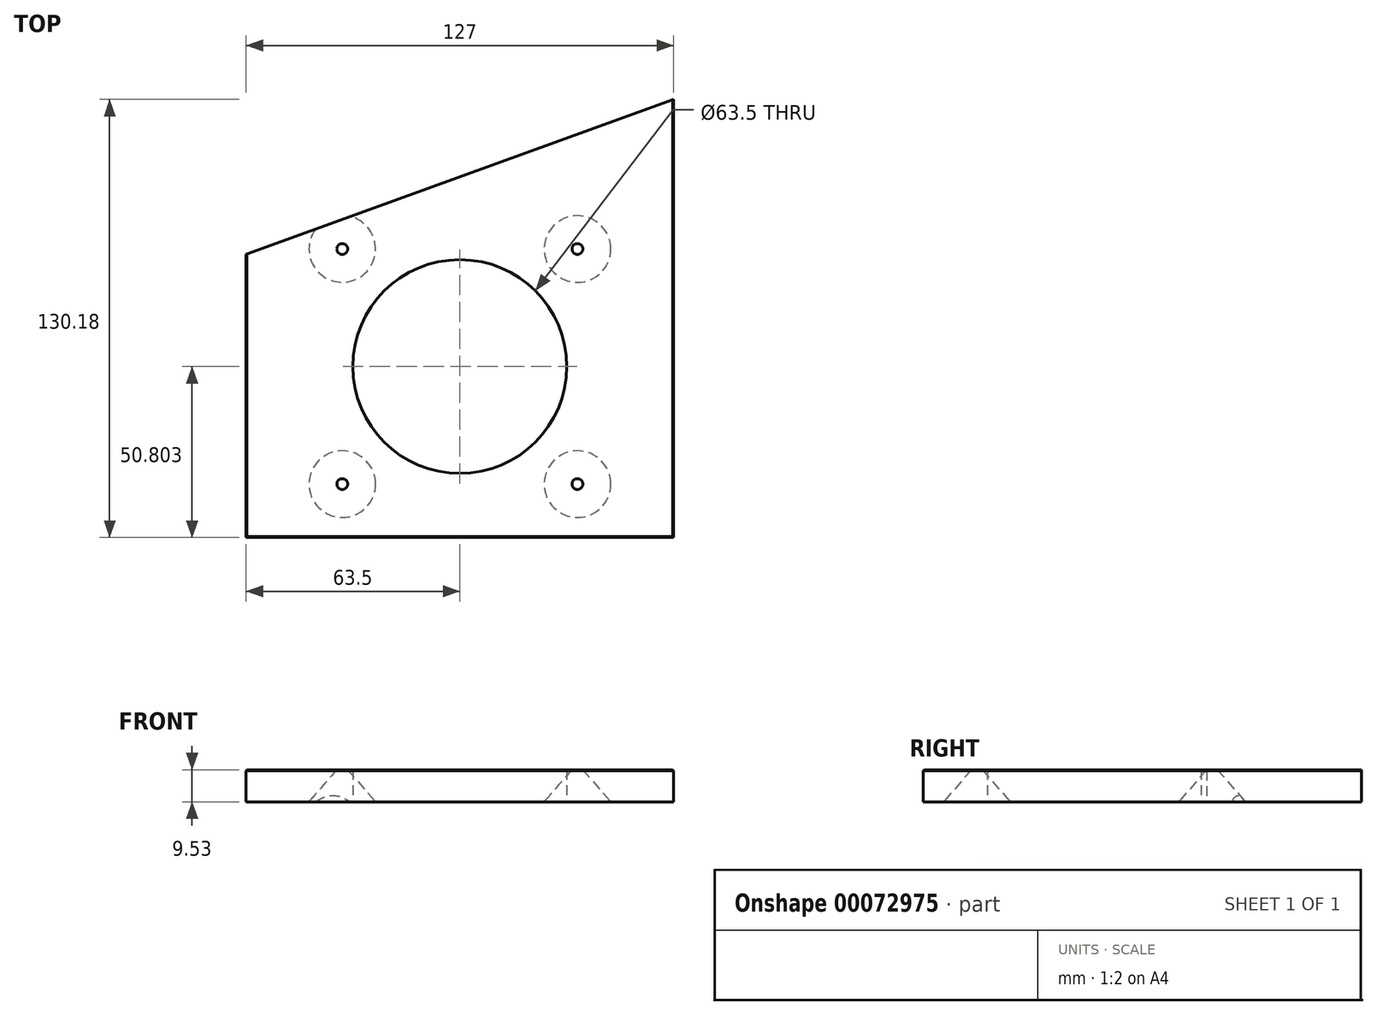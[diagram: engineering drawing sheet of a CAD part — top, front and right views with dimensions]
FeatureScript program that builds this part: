
annotation { "Feature Type Name" : "Feature", "Feature Type Description" : "" }
export const myFeature = defineFeature(function(context is Context, id is Id, definition is map)
    precondition{}
    {
        {
            var Q0;
            Q0=qCreatedBy(makeId("Top.planeOp"),FACE);
            var sketch = newSketch(context, id + "F0", { "sketchPlane" : qUnion([Q0])});
            skLineSegment(sketch, "E0.rect.bottom", {"start": v(63.5, -65.09) * mm, "end": v(-63.5, -65.09) * mm});
            skLineSegment(sketch, "E0.rect.left", {"start": v(63.5, -65.09) * mm, "end": v(63.5, 65.09) * mm});
            skLineSegment(sketch, "E0.rect.right", {"start": v(-63.5, -65.09) * mm, "end": v(-63.5, 19.05) * mm});
            skPoint(sketch, "E0.rect.middle", {"position": v(0, 0) * mm});
            skLineSegment(sketch, "E1", {"start": v(63.5, 65.09) * mm, "end": v(-63.5, 19.05) * mm});
            skLineSegment(sketch, "E2.0", {"start": v(-31.75, -65.09) * mm, "end": v(-31.75, 19.05) * mm, "construction": true});
            skLineSegment(sketch, "E3.0", {"start": v(31.75, -65.09) * mm, "end": v(31.75, 65.09) * mm, "construction": true});
            skLineSegment(sketch, "E4.0", {"start": v(63.5, -46.04) * mm, "end": v(-63.5, -46.04) * mm, "construction": true});
            skLineSegment(sketch, "E5.0", {"start": v(63.5, 17.46) * mm, "end": v(-63.5, 17.46) * mm, "construction": true});
            skLineSegment(sketch, "E6", {"start": v(31.75, 17.46) * mm, "end": v(-31.75, -46.04) * mm});
            skLineSegment(sketch, "E7", {"start": v(-31.75, 17.46) * mm, "end": v(31.75, -46.04) * mm});
            skPoint(sketch, "E8", {"position": v(0, -14.29) * mm});
            skCircle(sketch, "E9", {"center": v(0, -14.29) * mm, "radius": 31.75 * mm});
            skSolve(sketch);
        }
        {
            var Q0;
            Q0=makeQuery(id+"F0.imprint","IMPRINT",FACE,{"disambiguationData":[TD([[makeQuery(id+"F0.imprint","IMPRINT",EDGE,{"derivedFrom":sQuery(id+"F0.wireOp",EDGE,"E0.rect.bottom")}),-1.0]])]});
            extrude(context, id + "F1", {"entities" : qUnion([Q0]), "depth" : 9.52 * mm});
        }
        {
            var Q0;
            Q0=makeQuery(id+"F1.opExtrude","CAP_FACE",FACE,{"disambiguationData":[OSD([sQuery(id+"F0.wireOp",EDGE,"E0.rect.bottom"),sQuery(id+"F0.wireOp",EDGE,"E0.rect.left"),sQuery(id+"F0.wireOp",EDGE,"E0.rect.right"),sQuery(id+"F0.wireOp",EDGE,"E1"),sQuery(id+"F0.wireOp",EDGE,"E9")])],"isStart":false});
            var sketch = newSketch(context, id + "F2", { "sketchPlane" : qUnion([Q0])});
            skCircle(sketch, "E10.0", {"center": v(0, -14.29) * mm, "radius": 31.75 * mm});
            skLineSegment(sketch, "E11.bottom", {"start": v(-34.93, 20.64) * mm, "end": v(34.92, 20.64) * mm, "construction": true});
            skLineSegment(sketch, "E11.top", {"start": v(-34.93, -49.21) * mm, "end": v(34.92, -49.21) * mm, "construction": true});
            skLineSegment(sketch, "E11.left", {"start": v(-34.93, 20.64) * mm, "end": v(-34.93, -49.21) * mm, "construction": true});
            skLineSegment(sketch, "E11.right", {"start": v(34.92, 20.64) * mm, "end": v(34.92, -49.21) * mm, "construction": true});
            skCircle(sketch, "E12", {"center": v(-34.93, 20.64) * mm, "radius": 3.84 * mm});
            skCircle(sketch, "E13", {"center": v(34.93, 20.64) * mm, "radius": 3.84 * mm});
            skCircle(sketch, "E14", {"center": v(34.93, -49.21) * mm, "radius": 3.84 * mm});
            skCircle(sketch, "E15", {"center": v(-34.93, -49.21) * mm, "radius": 3.84 * mm});
            skSolve(sketch);
        }
        {
            var Q0;
            Q0=makeQuery(id+"F1.opExtrude","CAP_FACE",FACE,{"disambiguationData":[OSD([sQuery(id+"F0.wireOp",EDGE,"E0.rect.bottom"),sQuery(id+"F0.wireOp",EDGE,"E0.rect.left"),sQuery(id+"F0.wireOp",EDGE,"E0.rect.right"),sQuery(id+"F0.wireOp",EDGE,"E1"),sQuery(id+"F0.wireOp",EDGE,"E9")])],"isStart":true});
            var sketch = newSketch(context, id + "F3", { "sketchPlane" : qUnion([Q0])});
            skPoint(sketch, "E16.0", {"position": v(-34.93, 49.21) * mm});
            skPoint(sketch, "E17.0", {"position": v(34.92, 49.21) * mm});
            skPoint(sketch, "E18.0", {"position": v(34.92, -20.64) * mm});
            skPoint(sketch, "E19.0", {"position": v(-34.93, -20.64) * mm});
            skSolve(sketch);
        }
        {
            var Q0;
            Q0=sQuery(id+"F3.wireOp",VERTEX,"E16.0");
            var Q1;
            Q1=sQuery(id+"F3.wireOp",VERTEX,"E17.0");
            var Q2;
            Q2=sQuery(id+"F3.wireOp",VERTEX,"E18.0");
            var Q3;
            Q3=sQuery(id+"F3.wireOp",VERTEX,"E19.0");
            var Q4;
            Q4=makeQuery(id+"F1.opExtrude","SWEPT_BODY",BODY,{"disambiguationData":[OSD([sQuery(id+"F0.wireOp",EDGE,"E0.rect.bottom"),sQuery(id+"F0.wireOp",EDGE,"E0.rect.left"),sQuery(id+"F0.wireOp",EDGE,"E0.rect.right"),sQuery(id+"F0.wireOp",EDGE,"E1"),sQuery(id+"F0.wireOp",EDGE,"E9")])]});
            hole(context, id + "F4", {"style" : HoleStyle.C_SINK, "endStyle" : HoleEndStyle.THROUGH, "holeDiameter" : ((5 / 16) - 0.01) * mm, "cSinkDiameter" : 19.79 * mm, "cSinkAngle" : 82 * degree, "startFromSketch" : true, "locations" : qUnion([Q0, Q1, Q2, Q3]), "scope" : qUnion([Q4]), "isTappedThrough" : true});
        }
        {
            var Q0;
            Q0=makeQuery(id+"F1.opExtrude","CAP_EDGE",EDGE,{"disambiguationData":[OSD([sQuery(id+"F0.wireOp",EDGE,"E0.rect.right")])],"isStart":false});
            var Q1;
            Q1=makeQuery(id+"F1.opExtrude","CAP_EDGE",EDGE,{"disambiguationData":[OSD([sQuery(id+"F0.wireOp",EDGE,"E0.rect.bottom")])],"isStart":false});
            var Q2;
            Q2=makeQuery(id+"F1.opExtrude","CAP_EDGE",EDGE,{"disambiguationData":[OSD([sQuery(id+"F0.wireOp",EDGE,"E0.rect.left")])],"isStart":false});
            chamfer(context, id + "F5", {"entities" : qUnion([Q0, Q1, Q2]), "width" : ((3 / 8) - .125) * mm, "tangentPropagation" : true});
        }
        {
            var Q0;
            Q0=sQuery(id+"F2.wireOp",EDGE,"E11.top");
            var Q1;
            Q1=qCreatedBy(makeId("Front.planeOp"),FACE);
            cPlane(context, id + "F6", {"entities" : qUnion([Q0, Q1]), "cplaneType" : CPlaneType.LINE_ANGLE, "offset" : 25.4 * mm, "angle" : 0 * degree, "width" : 152.4 * mm, "height" : 152.4 * mm});
        }
    });
